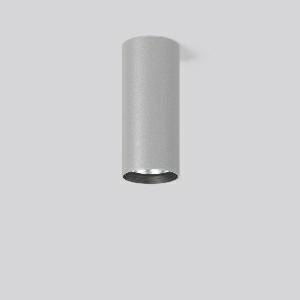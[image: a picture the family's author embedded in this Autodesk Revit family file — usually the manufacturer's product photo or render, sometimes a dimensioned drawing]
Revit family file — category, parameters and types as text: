
# Revit family: heledon_mini_a_931202_004_1cb7
name_source: partatom
category: Lighting Fixtures
units: mm (PartAtom-declared; Revit-internal decimal feet)

## family parameters
Cut with Voids When Loaded = No
Host = Face
Light Source = No
Part Type = Normal
Room Calculation Point = No
Round Connector Dimension = Use Diameter
Shared = No

## types (1)
- HELEDON mini A (1 x LED Modul 930, 2550 lm, 3000)
    Apparent Load = 20 VA
    Approval mark = CE
    CIE Flux Codes = 95 99 100 100 100
    Color Rendering = 90
    Color Temperature = 3000
    Default Elevation = 1800 mm
    Description = Series: HELEDON mini
Cylindrical surface-mounted downlight. Housing: die-cast aluminium, powder-coated. Internal ceiling frame polycarbonate with bayonet mounting. Black plastic ring and recessed LED to prevent glare from the side. Optical assembly with reflector made of MIRO-Silver with 98% total light reflection for outstanding efficiency - can be changed without tools. Best colour rendering index Ra>90. Suitable for Ceiling mounting. Easy installation with a separate ceiling frame with bayonet mounting and plug connection. Driver integrated. Connected via plug-in connector. High quality converter without flickering and stroboscopic effect. The following accessories can be mounted without use of tools: interchangeable lenses, decorative glasses, honeycomb louvre, clear and frosted diffusers, white interchangeable plastic ring. 
Colour: silver
Diameter: 87 mm
Height: 197 mm
Lamp: LED
Socket: without socket
Colour temperature: 3000K
Colour rendering index (CRI): 92
System power: 20 W
Rated luminous flux: 2550 lm
Luminous efficiency: 128 lm/W
Control gear: Regulated power supply
Protection class: I
Type of protection: IP 20
    Height = 197 mm
    Lamp = 1 x LED Modul 930
    Lamp Light Flux = 2550 lm
    Lamp count = 1
    Length = 87 mm
    Lifetime = 50000 h
    Luminous efficacy = 128 lm/W
    Manufacturer = RZB
    ModVariant = No
    Model = 931202.004
    Mounting Place = Ceiling
    Mounting Type = Surface mounted
    Number of Poles = 1
    OnlyDefault = Yes
    Power Factor = 1
    Product Name = HELEDON mini A
    Product group = Surface mounted downlights
    ProductGroupID = 302
    Protection Class = Protection class I
    Protection Degree = IP 20
    RLX_Detail_Level = 1
    RLX_Emergency_Light_Flux = 0 lm
    RLX_Emergency_Type = 0
    RLX_Emergency_Type_DB = No
    RlxData = <blob elided: 108269 chars, md5=beeda30f>
    Socket = socket
    Standby Power = 0 W
    System Light Flux = 2550 lm
    System Power = 20 W
    Type Comments = Product without accessories
    Type Image = 931188.004.jpg
    URL = http://relux.com
    VarID = ---
    Voltage = 230 V
    Voltage Range = 220-240 V
    Weight = 0.00 kg
    Width = 0 mm  [stored 0 ft]

note: [stored X ft] marks values corroborated as IEEE doubles in the binary element streams (Revit-internal decimal feet)

## geometry (parser evidence)
native form markers: Blend x4, Sweep x9
no freeform markers — native parametric forms only
